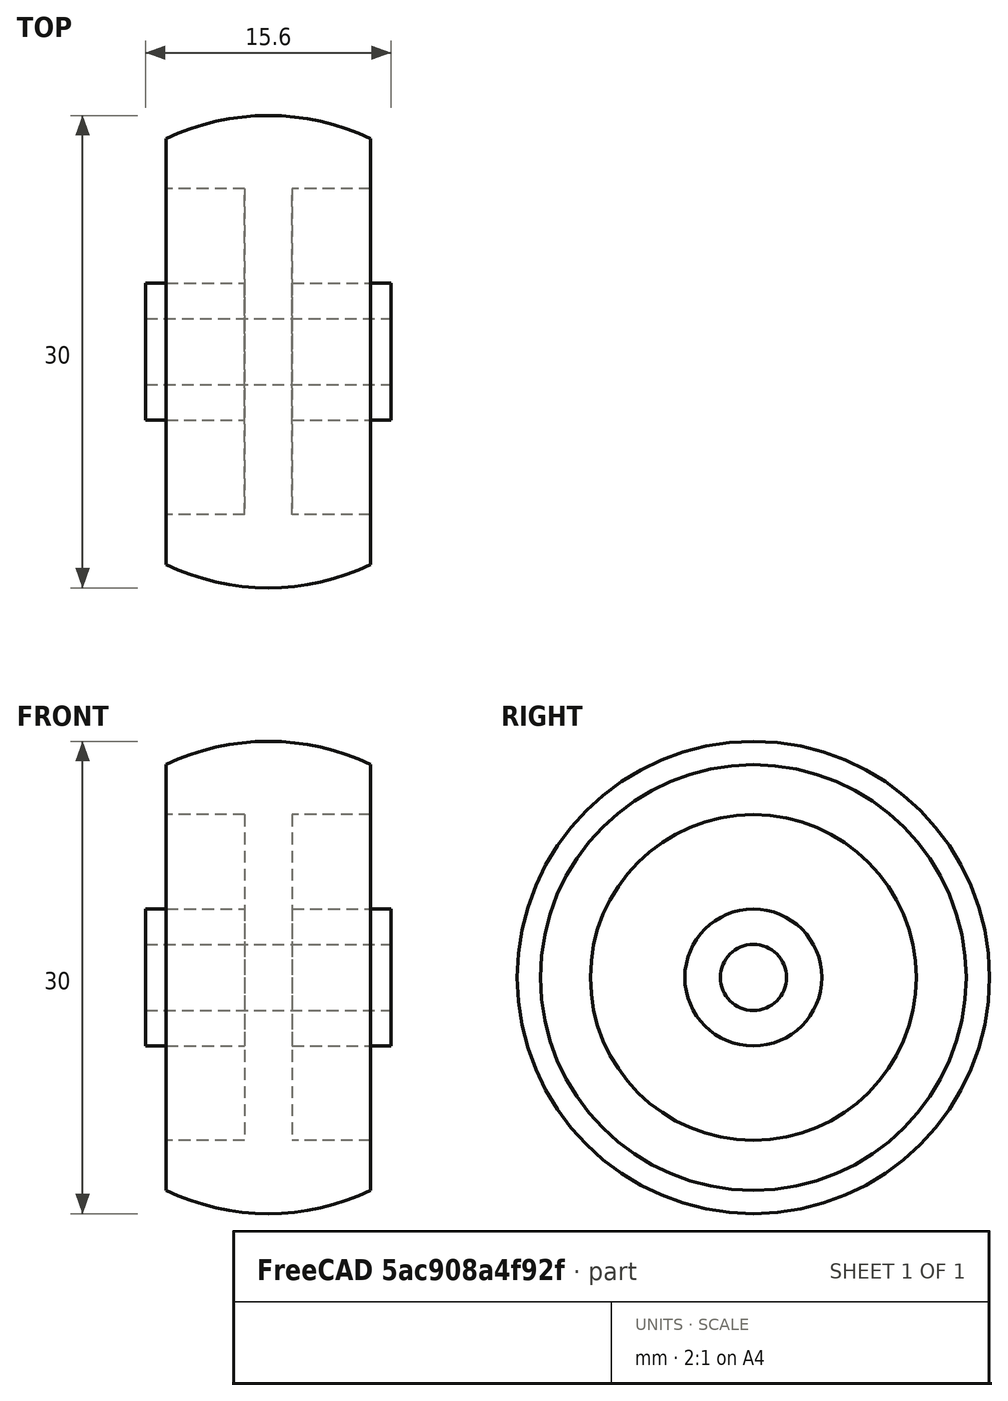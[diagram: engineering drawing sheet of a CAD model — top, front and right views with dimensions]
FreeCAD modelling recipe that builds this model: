
FCSTD DOCUMENT  (FreeCAD 0.17R13522 (Git))
Label: Caster-40mm_Wheel_30mm
License: All rights reserved
LicenseURL: http://en.wikipedia.org/wiki/All_rights_reserved
objects: Sketcher::SketchObject×1, PartDesign::Revolution×1, PartDesign::Body×1
note: 4 computed .brp shape members not serialized (recipe doc carries the construction recipe); baked Part::Feature solids carry a one-line shape summary decoded from their .brp

FEATURE [Sketcher::SketchObject] Sketch
  MapMode = 5
  Placement = pos=(0,0,0) rot=(1,0,0;1.5708rad)
  Support = -> [XZ_Plane]
  sketch-geometry (12):
    g0: LineSegment StartX=-7.8 StartY=2.1 StartZ=0 EndX=7.8 EndY=2.1 EndZ=0
    g1: LineSegment StartX=-7.8 StartY=2.1 StartZ=0 EndX=-7.8 EndY=4.35 EndZ=0
    g2: LineSegment StartX=-7.8 StartY=4.35 StartZ=0 EndX=-1.5 EndY=4.35 EndZ=0
    g3: LineSegment StartX=-1.5 StartY=4.35 StartZ=0 EndX=-1.5 EndY=10.35 EndZ=0
    g4: LineSegment StartX=-1.5 StartY=10.35 StartZ=0 EndX=-6.5 EndY=10.35 EndZ=0
    g5: LineSegment StartX=-6.5 StartY=10.35 StartZ=0 EndX=-6.5 EndY=13.5185 EndZ=0
    g6: LineSegment StartX=6.5 StartY=13.5185 StartZ=0 EndX=6.5 EndY=10.35 EndZ=0
    g7: LineSegment StartX=6.5 StartY=10.35 StartZ=0 EndX=1.5 EndY=10.35 EndZ=0
    g8: LineSegment StartX=1.5 StartY=10.35 StartZ=0 EndX=1.5 EndY=4.35 EndZ=0
    g9: LineSegment StartX=1.5 StartY=4.35 StartZ=0 EndX=7.8 EndY=4.35 EndZ=0
    g10: LineSegment StartX=7.8 StartY=4.35 StartZ=0 EndX=7.8 EndY=2.1 EndZ=0
    g11: ArcOfCircle CenterX=0 CenterY=0 CenterZ=0 NormalX=0 NormalY=0 NormalZ=1 AngleXU=0 Radius=15 StartAngle=1.12261 EndAngle=2.01898
  constraints (36):
    c: Symmetric(g0,g0,g-2)
    c: Coincident(g1,g0)
    c: Vertical(g1)
    c: Coincident(g1,g2)
    c: Horizontal(g2)
    c: Coincident(g2,g3)
    c: Vertical(g3)
    c: Coincident(g3,g4)
    c: Horizontal(g4)
    c: Coincident(g4,g5)
    c: Vertical(g5)
    c: Vertical(g6)
    c: Coincident(g6,g7)
    c: Horizontal(g7)
    c: Coincident(g7,g8)
    c: Vertical(g8)
    c: Coincident(g8,g9)
    c: Horizontal(g9)
    c: Coincident(g9,g10)
    c: Coincident(g10,g0)
    c: Vertical(g10)
    c: Equal(g1,g10)
    c: Equal(g5,g6)
    c: Equal(g7,g4)
    c: Symmetric(g2,g8,g-2)
    c: PointOnObject(g11,g-2)
    c: Coincident(g11,g5)
    c: Coincident(g11,g6)
    c: DistanceX(g5,g6) = 13
    c: DistanceX(g0,g0) = 15.6
    c: DistanceX(g2,g8) = 3
    c: DistanceY(g-1,g0) = 2.1
    c: DistanceY(g9) = 4.35
    c: DistanceY(g8,g8) = 6
    c: Radius(g11) = 15
    c: Coincident(g11,g-1)
FEATURE [PartDesign::Revolution] Revolution
  Angle = 360
  Axis = (1,0,0)
  Base = (0,0,0)
  Placement = pos=(0,0,0) rot=(1,0,0;1.5708rad)
  Profile = -> Sketch
  ReferenceAxis = -> X_Axis
FEATURE [PartDesign::Body] Body
  Group = -> [Sketch,Revolution]
  Origin = -> Origin
  Tip = -> Revolution
